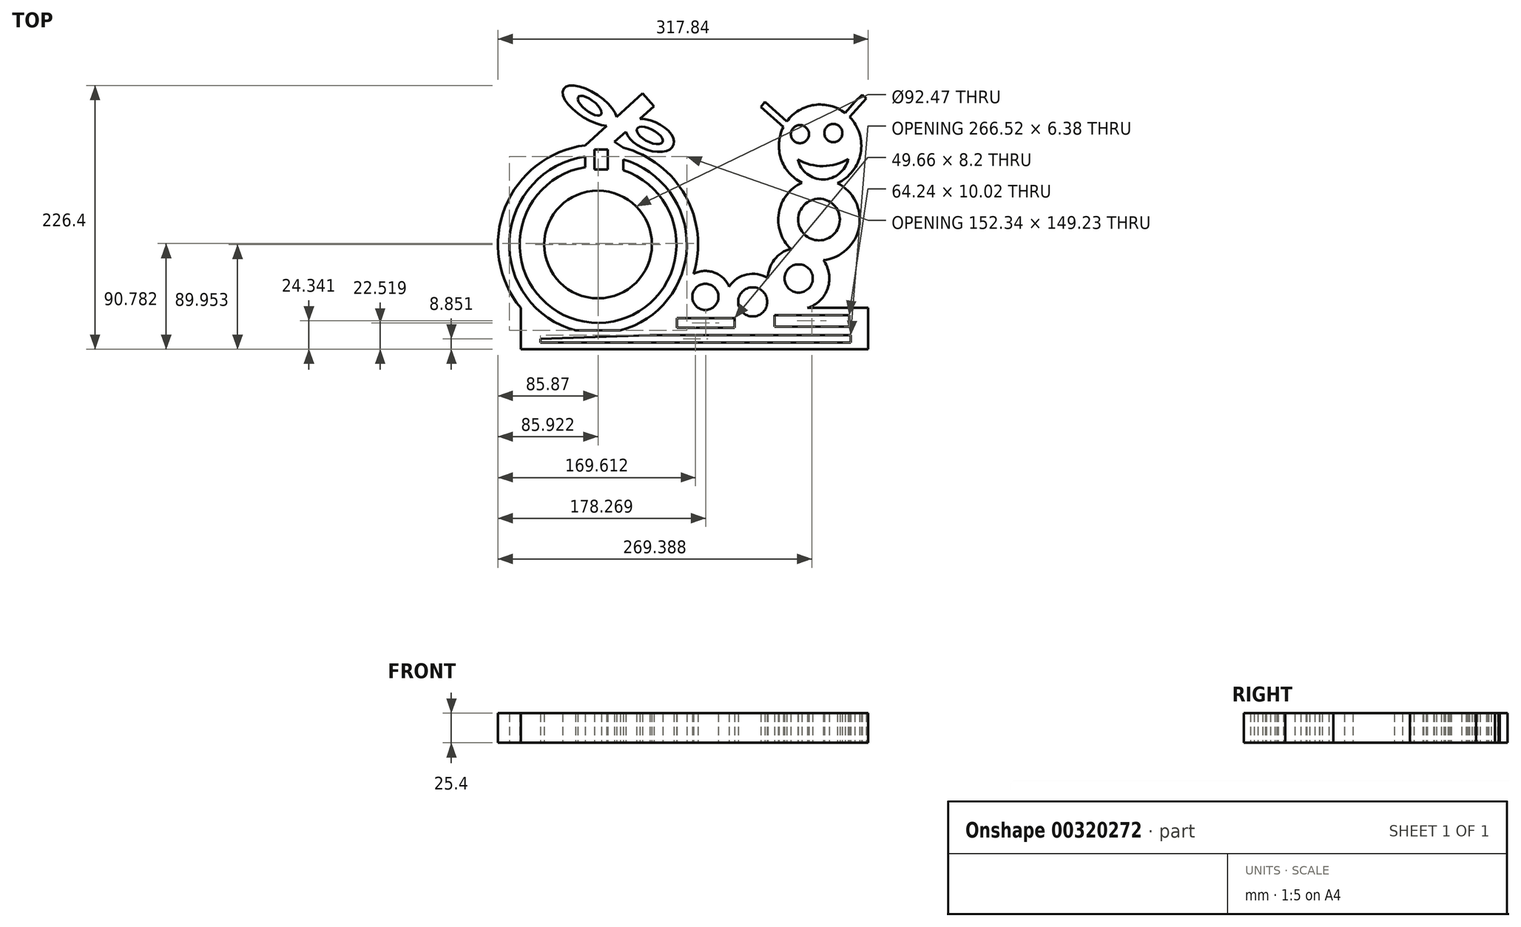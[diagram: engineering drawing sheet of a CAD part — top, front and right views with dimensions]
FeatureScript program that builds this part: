
annotation { "Feature Type Name" : "Feature", "Feature Type Description" : "" }
export const myFeature = defineFeature(function(context is Context, id is Id, definition is map)
    precondition{}
    {
        {
            var Q0;
            Q0=qCreatedBy(makeId("Top.planeOp"),FACE);
            var sketch = newSketch(context, id + "F0", { "sketchPlane" : qUnion([Q0])});
            skArc(sketch, "E0", {"start": v(74.44, -21.02) * mm, "mid": v(61.6, -8.9) * mm, "end": v(43.99, -9.97) * mm});
            skArc(sketch, "E1", {"start": v(107.73, -13.9) * mm, "mid": v(89.6, -10.57) * mm, "end": v(74.44, -21.02) * mm});
            skArc(sketch, "E2", {"start": v(127.24, 11.45) * mm, "mid": v(113.2, 2.07) * mm, "end": v(107.73, -13.9) * mm});
            skArc(sketch, "E3", {"start": v(136.8, 68.22) * mm, "mid": v(117.12, 42.35) * mm, "end": v(127.24, 11.45) * mm});
            skArc(sketch, "E4", {"start": v(167.34, 67.78) * mm, "mid": v(187.32, 93.46) * mm, "end": v(177.87, 124.6) * mm});
            skLineSegment(sketch, "E5", {"start": v(105.3, 137.56) * mm, "end": v(124, 120.83) * mm});
            skLineSegment(sketch, "E6", {"start": v(121, 115.94) * mm, "end": v(101.64, 133.26) * mm});
            skLineSegment(sketch, "E7", {"start": v(101.64, 133.26) * mm, "end": v(105.3, 137.56) * mm});
            skLineSegment(sketch, "E8", {"start": v(182.42, 137.56) * mm, "end": v(173.94, 128.08) * mm});
            skLineSegment(sketch, "E9", {"start": v(192.23, 140.65) * mm, "end": v(188.77, 143.75) * mm});
            skLineSegment(sketch, "E10", {"start": v(188.77, 143.75) * mm, "end": v(182.42, 137.56) * mm});
            skLineSegment(sketch, "E11", {"start": v(192.23, 140.65) * mm, "end": v(177.87, 124.6) * mm});
            skPoint(sketch, "E12.orphan", {"position": v(195.7, 137.56) * mm});
            skPoint(sketch, "E13.orphan", {"position": v(177.92, 117.7) * mm});
            skLineSegment(sketch, "E14", {"start": v(-16.33, 88.2) * mm, "end": v(-16.33, 82.06) * mm});
            skLineSegment(sketch, "E15", {"start": v(-16.33, 82.06) * mm, "end": v(-16.33, 88.2) * mm});
            skLineSegment(sketch, "E16", {"start": v(-45, 104.02) * mm, "end": v(-30.6, 117.1) * mm});
            skLineSegment(sketch, "E17", {"start": v(0, 144.93) * mm, "end": v(10.04, 133.89) * mm});
            skLineSegment(sketch, "E18", {"start": v(10.04, 133.89) * mm, "end": v(-2.05, 123) * mm});
            skEllipticalArc(sketch, "E19", {});
            skEllipticalArc(sketch, "E20", {});
            skArc(sketch, "E21", {"start": v(-49.05, 81.58) * mm, "mid": v(-43.74, -51.94) * mm, "end": v(-16.33, 78.85) * mm});
            skLineSegment(sketch, "E22.trimOffspring", {"start": v(-22.31, 124.64) * mm, "end": v(0, 144.93) * mm});
            skLineSegment(sketch, "E23.trimOffspring", {"start": v(-14.16, 112.08) * mm, "end": v(-24.02, 103.2) * mm});
            skArc(sketch, "E24.trimOffspring", {"start": v(-49.05, 100.33) * mm, "mid": v(-117.93, 46.87) * mm, "end": v(-104.55, -39.28) * mm});
            skPoint(sketch, "E25.start.orphan", {"position": v(-27.2, 100.33) * mm});
            skPoint(sketch, "E26", {"position": v(152.53, 98.6) * mm});
            skLineSegment(sketch, "E27", {"start": v(-16.33, 98.21) * mm, "end": v(-24.02, 103.2) * mm});
            skArc(sketch, "E28.trimOffspring", {"start": v(155.23, 1.75) * mm, "mid": v(186.01, 30.23) * mm, "end": v(167.34, 67.78) * mm});
            skLineSegment(sketch, "E29", {"start": v(-49.05, 84.67) * mm, "end": v(-49.05, 81.58) * mm});
            skLineSegment(sketch, "E30", {"start": v(-16.33, 82.06) * mm, "end": v(-16.33, 78.85) * mm});
            skPoint(sketch, "E31.trimOffspring.start.orphan", {"position": v(-90.54, -56.98) * mm});
            skPoint(sketch, "E32.start.orphan", {"position": v(127.5, 117.7) * mm});
            skLineSegment(sketch, "E33", {"start": v(8.1, -57.28) * mm, "end": v(8.46, -56.98) * mm});
            skArc(sketch, "E34.trimOffspring", {"start": v(121, 115.94) * mm, "mid": v(118.95, 88.79) * mm, "end": v(136.8, 68.22) * mm});
            skArc(sketch, "E35.trimOffspring", {"start": v(173.94, 128.08) * mm, "mid": v(147.45, 134.93) * mm, "end": v(124, 120.83) * mm});
            skArc(sketch, "E36", {"start": v(-49.05, 90.6) * mm, "mid": v(-114.25, 19.35) * mm, "end": v(-57.29, -58.64) * mm});
            skArc(sketch, "E37.trimOffspring", {"start": v(-18.97, -58.64) * mm, "mid": v(38.1, 13.78) * mm, "end": v(-16.33, 88.2) * mm});
            skLineSegment(sketch, "E38.trimOffspring", {"start": v(-49.05, 90.6) * mm, "end": v(-49.05, 84.67) * mm});
            skPoint(sketch, "E39.end.orphan", {"position": v(-49.05, 98.21) * mm});
            skLineSegment(sketch, "E40", {"start": v(-45, 104.02) * mm, "end": v(-49.05, 100.33) * mm});
            skCircle(sketch, "E41", {"center": v(-38.13, 15.15) * mm, "radius": 46.23 * mm});
            skLineSegment(sketch, "E42.bottom", {"start": v(-41.12, 96.7) * mm, "end": v(-29.73, 96.7) * mm});
            skLineSegment(sketch, "E42.top", {"start": v(-41.12, 79.38) * mm, "end": v(-29.73, 79.38) * mm});
            skLineSegment(sketch, "E42.left", {"start": v(-41.12, 96.7) * mm, "end": v(-41.12, 79.38) * mm});
            skLineSegment(sketch, "E42.right", {"start": v(-29.73, 96.7) * mm, "end": v(-29.73, 79.38) * mm});
            skEllipse(sketch, "E43", {"center": v(6.3, 108.8) * mm, "majorRadius": 12.32 * mm, "minorRadius": 5.42 * mm, "majorAxis": v(0.89, -0.47)});
            skEllipse(sketch, "E44", {"center": v(-45.32, 134.35) * mm, "majorRadius": 12.29 * mm, "minorRadius": 4.89 * mm, "majorAxis": v(0.79, -0.62)});
            skCircle(sketch, "E45", {"center": v(151.6, 36.54) * mm, "radius": 17.88 * mm});
            skCircle(sketch, "E46", {"center": v(134.1, -14) * mm, "radius": 12.11 * mm});
            skCircle(sketch, "E47", {"center": v(94.65, -34.13) * mm, "radius": 12.5 * mm});
            skCircle(sketch, "E48", {"center": v(135.2, 109.91) * mm, "radius": 7.75 * mm});
            skCircle(sketch, "E49", {"center": v(163.9, 110.82) * mm, "radius": 7.79 * mm});
            skArc(sketch, "E50", {"start": v(133.37, 88.04) * mm, "mid": v(155.07, 82.46) * mm, "end": v(176.65, 88.5) * mm});
            skArc(sketch, "E51", {"start": v(133.37, 88.04) * mm, "mid": v(155.2, 71) * mm, "end": v(176.65, 88.5) * mm});
            skArc(sketch, "E52", {"start": v(44.05, -9.93) * mm, "mid": v(36.87, 57.1) * mm, "end": v(-16.48, 98.3) * mm});
            skLineSegment(sketch, "E53.trimOffspring", {"start": v(-57.29, -58.64) * mm, "end": v(-18.97, -58.64) * mm});
            skLineSegment(sketch, "E54.trimOffspring", {"start": v(5.9, -58.64) * mm, "end": v(6.44, -58.64) * mm});
            skLineSegment(sketch, "E55", {"start": v(6.44, -58.64) * mm, "end": v(6.44, -58.64) * mm});
            skArc(sketch, "E56", {"start": v(43.99, -9.97) * mm, "mid": v(36.87, 56.97) * mm, "end": v(-16.33, 98.21) * mm});
            skCircle(sketch, "E57", {"center": v(54.02, -29.79) * mm, "radius": 11.23 * mm});
            skLineSegment(sketch, "E58.top", {"start": v(-104.55, -74.8) * mm, "end": v(193.84, -74.8) * mm});
            skLineSegment(sketch, "E58.left", {"start": v(-104.55, -39.28) * mm, "end": v(-104.55, -74.8) * mm});
            skLineSegment(sketch, "E58.right", {"start": v(193.84, -39.28) * mm, "end": v(193.84, -74.8) * mm});
            skLineSegment(sketch, "E59.trimOffspring", {"start": v(141.61, -39.28) * mm, "end": v(193.84, -39.28) * mm});
            skArc(sketch, "E60.trimOffspring", {"start": v(141.61, -39.28) * mm, "mid": v(159.12, -22.32) * mm, "end": v(155.23, 1.75) * mm});
            skArc(sketch, "E61.trimOffspring", {"start": v(-48.98, 100.4) * mm, "mid": v(-117.98, 46.9) * mm, "end": v(-104.55, -39.37) * mm});
            skPoint(sketch, "E62.orphan", {"position": v(-84.72, -56.98) * mm});
            skLineSegment(sketch, "E63.bottom", {"start": v(6.26, -62.76) * mm, "end": v(178.87, -62.76) * mm});
            skLineSegment(sketch, "E63.top", {"start": v(-87.65, -69.14) * mm, "end": v(178.87, -69.14) * mm});
            skLineSegment(sketch, "E63.left", {"start": v(-87.65, -65.95) * mm, "end": v(-87.65, -69.14) * mm});
            skLineSegment(sketch, "E63.right", {"start": v(178.87, -62.76) * mm, "end": v(178.87, -69.14) * mm});
            skLineSegment(sketch, "E64.bottom", {"start": v(113.27, -45.45) * mm, "end": v(177.5, -45.45) * mm});
            skLineSegment(sketch, "E64.top", {"start": v(113.27, -55.47) * mm, "end": v(177.5, -55.47) * mm});
            skLineSegment(sketch, "E64.left", {"start": v(113.27, -45.45) * mm, "end": v(113.27, -55.47) * mm});
            skLineSegment(sketch, "E64.right", {"start": v(177.5, -45.45) * mm, "end": v(177.5, -55.47) * mm});
            skLineSegment(sketch, "E65.bottom", {"start": v(29.44, -48.18) * mm, "end": v(79.1, -48.18) * mm});
            skLineSegment(sketch, "E65.top", {"start": v(29.44, -56.38) * mm, "end": v(79.1, -56.38) * mm});
            skLineSegment(sketch, "E65.left", {"start": v(29.44, -48.18) * mm, "end": v(29.44, -56.38) * mm});
            skLineSegment(sketch, "E65.right", {"start": v(79.1, -48.18) * mm, "end": v(79.1, -56.38) * mm});
            skLineSegment(sketch, "E66", {"start": v(6.26, -62.76) * mm, "end": v(-87.65, -65.95) * mm});
            skPoint(sketch, "E67.orphan", {"position": v(-87.65, -62.76) * mm});
            const initialGuessF0  = {"E19": [-0.04532485455273585, 0.13434642553328338, 0.8411784252652177, -0.5407576692644577, 0.02656926850409278, 0.011352996176210762, 0.38683287968341235, 5.668584686066687], "E20": [0.006291836500167847, 0.10880415141582489, -0.9216355285500892, 0.38805663570437465, 0.02194031267228592, 0.012320454163056162, 0.4101280656357543, 5.357445328832655]};
            skSetInitialGuess(sketch, initialGuessF0);
            skSolve(sketch);
        }
        {
            var Q0;
            {var subQ0=sQuery(id+"F0.wireOp",EDGE,"E0");var subQ1=sQuery(id+"F0.wireOp",EDGE,"agBBpf9L-HDxB-052C-k031-Bi3RSpg8Mt1g");var subQ2=makeQuery(id+"F0.imprint","INTERSECT",VERTEX,{"disambiguationData":[OD(0.0)],"derivedFrom":[subQ1,subQ0]});Q0=makeQuery(id+"F0.imprint","IMPRINT",FACE,{"disambiguationData":[TD([[makeQuery(id+"F0.imprint","IMPRINT",EDGE,{"disambiguationData":[TD([[subQ2,-1.0]])],"derivedFrom":subQ1}),1.0]])]});}
            var Q1;
            Q1=makeQuery(id+"F0.imprint","IMPRINT",FACE,{"disambiguationData":[TD([[makeQuery(id+"F0.imprint","IMPRINT",EDGE,{"derivedFrom":sQuery(id+"F0.wireOp",EDGE,"E21")}),1.0]])]});
            var Q2;
            {var subQ4=sQuery(id+"F0.wireOp",EDGE,"E9");Q2=makeQuery(id+"F0.imprint","IMPRINT",FACE,{"disambiguationData":[TD([[makeQuery(id+"F0.imprint","IMPRINT",EDGE,{"derivedFrom":subQ4}),1.0]])]});}
            var Q3;
            {var subQ5=sQuery(id+"F0.wireOp",EDGE,"E7");Q3=makeQuery(id+"F0.imprint","IMPRINT",FACE,{"disambiguationData":[TD([[makeQuery(id+"F0.imprint","IMPRINT",EDGE,{"derivedFrom":subQ5}),-1.0]])]});}
            var Q4;
            {var subQ5=sQuery(id+"F0.wireOp",EDGE,"xMkvBLLg-xaSq-j8oh-MrKd-SSDycmBC8dnO");Q4=makeQuery(id+"F0.imprint","IMPRINT",FACE,{"disambiguationData":[TD([[makeQuery(id+"F0.imprint","IMPRINT",EDGE,{"derivedFrom":subQ5}),1.0]])]});}
            var Q5;
            {var subQ5=sQuery(id+"F0.wireOp",EDGE,"E32");Q5=makeQuery(id+"F0.imprint","IMPRINT",FACE,{"disambiguationData":[TD([[makeQuery(id+"F0.imprint","IMPRINT",EDGE,{"derivedFrom":subQ5}),-1.0]])]});}
            var Q6;
            {var subQ0=sQuery(id+"F0.wireOp",EDGE,"K9kmiR8Z-F2sR-8jnU-Q4AU-xC1HPNG77nRx");Q6=makeQuery(id+"F0.imprint","IMPRINT",FACE,{"disambiguationData":[TD([[makeQuery(id+"F0.imprint","IMPRINT",EDGE,{"derivedFrom":subQ0}),1.0]])]});}
            var Q7;
            {var subQ1=sQuery(id+"F0.wireOp",EDGE,"u855iF38-qQrI-NKxE-J6su-cf43kH7EnBoX");Q7=makeQuery(id+"F0.imprint","IMPRINT",FACE,{"disambiguationData":[TD([[makeQuery(id+"F0.imprint","IMPRINT",EDGE,{"derivedFrom":subQ1}),-1.0]])]});}
            var Q8;
            {var subQ15=sQuery(id+"F0.wireOp",EDGE,"E1");Q8=makeQuery(id+"F0.imprint","IMPRINT",FACE,{"disambiguationData":[TD([[makeQuery(id+"F0.imprint","IMPRINT",EDGE,{"derivedFrom":subQ15}),1.0]])]});}
            var Q9;
            {var subQ1=sQuery(id+"F0.wireOp",EDGE,"u855iF38-qQrI-NKxE-J6su-cf43kH7EnBoX");Q9=makeQuery(id+"F0.imprint","IMPRINT",FACE,{"disambiguationData":[TD([[makeQuery(id+"F0.imprint","IMPRINT",EDGE,{"derivedFrom":subQ1}),1.0]])]});}
            extrude(context, id + "F1", {"entities" : qUnion([Q0, Q1, Q2, Q3, Q4, Q5, Q6, Q7, Q8, Q9]), "depth" : 25.4 * mm});
        }
    });
